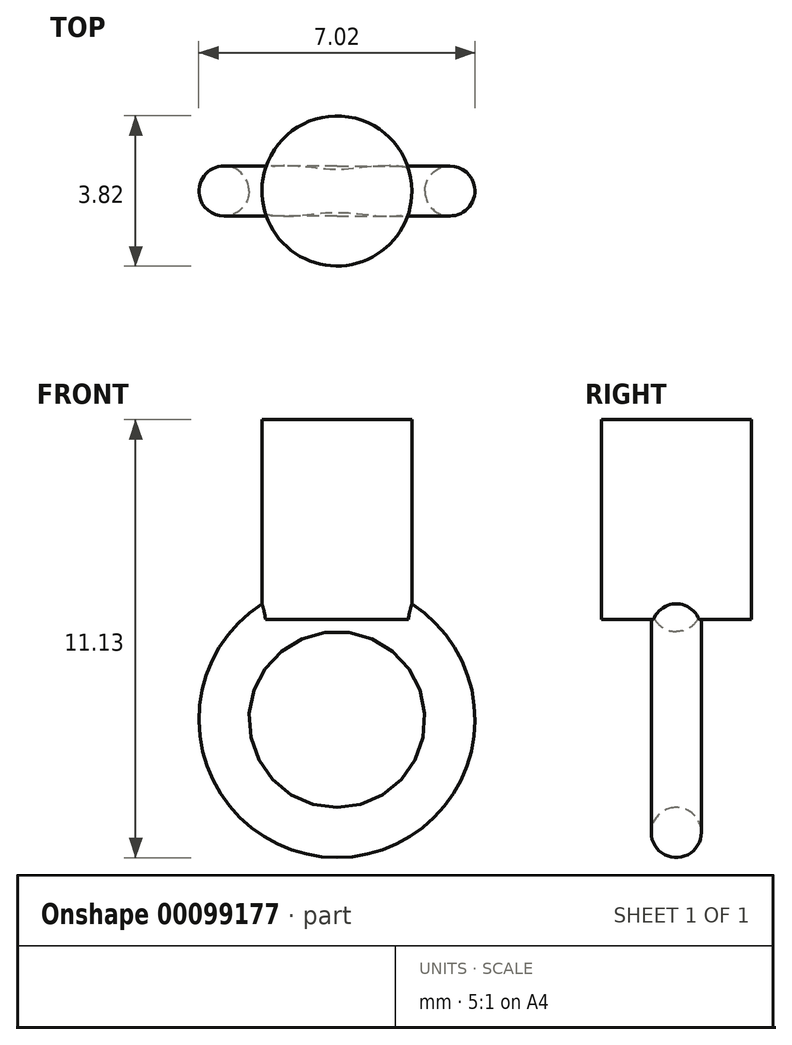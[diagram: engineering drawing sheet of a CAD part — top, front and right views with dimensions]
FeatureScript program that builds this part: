
annotation { "Feature Type Name" : "Feature", "Feature Type Description" : "" }
export const myFeature = defineFeature(function(context is Context, id is Id, definition is map)
    precondition{}
    {
        {
            var Q0;
            Q0=qCreatedBy(makeId("Top.planeOp"),FACE);
            var sketch = newSketch(context, id + "F0", { "sketchPlane" : qUnion([Q0])});
            skCircle(sketch, "E0", {"center": v(0, 0) * mm, "radius": 1.9 * mm});
            skSolve(sketch);
        }
        {
            var Q0;
            Q0=makeQuery(id+"F0.imprint","IMPRINT",FACE,{"disambiguationData":[TD([[makeQuery(id+"F0.imprint","IMPRINT",EDGE,{"derivedFrom":sQuery(id+"F0.wireOp",EDGE,"E0")}),1.0]])]});
            extrude(context, id + "F1", {"entities" : qUnion([Q0]), "depth" : 5.08 * mm});
        }
        {
            var Q0;
            Q0=qCreatedBy(makeId("Front.planeOp"),FACE);
            var sketch = newSketch(context, id + "F2", { "sketchPlane" : qUnion([Q0])});
            skLineSegment(sketch, "E1", {"start": v(0, 0) * mm, "end": v(0, -2.54) * mm, "construction": true});
            skCircle(sketch, "E2", {"center": v(0, -2.54) * mm, "radius": 2.54 * mm});
            skSolve(sketch);
        }
        {
            var Q0;
            Q0=qCreatedBy(makeId("Right.planeOp"),FACE);
            var sketch = newSketch(context, id + "F3", { "sketchPlane" : qUnion([Q0])});
            skLineSegment(sketch, "E3", {"start": v(0, 0) * mm, "end": v(0, 0.33) * mm, "construction": true});
            skCircle(sketch, "E4", {"center": v(0, 0.33) * mm, "radius": 0.64 * mm});
            skSolve(sketch);
        }
        {
            var Q0;
            Q0=makeQuery(id+"F3.imprint","IMPRINT",FACE,{"disambiguationData":[TD([[makeQuery(id+"F3.imprint","IMPRINT",EDGE,{"derivedFrom":sQuery(id+"F3.wireOp",EDGE,"E4")}),1.0]])]});
            var Q1;
            Q1=sQuery(id+"F2.wireOp",EDGE,"E2");
            revolve(context, id + "F4", {"operationType" : NewBodyOperationType.ADD, "entities" : qUnion([Q0]), "axis" : qUnion([Q1]), "revolveType" : RevolveType.FULL});
        }
    });
